FCSTD DOCUMENT  (FreeCAD 0.19R24276 (Git))
Label: Master_sketch_3_2
License: All rights reserved
LicenseURL: http://en.wikipedia.org/wiki/All_rights_reserved
objects: Sketcher::SketchObject×1, PartDesign::Body×1
note: 2 computed .brp shape members not serialized (recipe doc carries the construction recipe); baked Part::Feature solids carry a one-line shape summary decoded from their .brp

FEATURE [Sketcher::SketchObject] Sketch
  FullyConstrained = false
  MapMode = 5
  Support = -> [XY_Plane]
  sketch-geometry (199):
    g0: LineSegment StartX=-40 StartY=82 StartZ=0 EndX=40 EndY=82 EndZ=0
    g1: LineSegment StartX=40 StartY=82 StartZ=0 EndX=40 EndY=71 EndZ=0
    g2: LineSegment StartX=40 StartY=71 StartZ=0 EndX=-40 EndY=71 EndZ=0
    g3: LineSegment StartX=-40 StartY=71 StartZ=0 EndX=-40 EndY=82 EndZ=0
    g4: LineSegment StartX=-25 StartY=82 StartZ=0 EndX=-25 EndY=71 EndZ=0
    g5: LineSegment StartX=25 StartY=82 StartZ=0 EndX=25 EndY=71 EndZ=0
    g6: LineSegment StartX=-40 StartY=71 StartZ=0 EndX=-25 EndY=82 EndZ=0
    g7: LineSegment StartX=-40 StartY=82 StartZ=0 EndX=-25 EndY=71 EndZ=0
    g8: LineSegment StartX=25 StartY=71 StartZ=0 EndX=40 EndY=82 EndZ=0
    g9: LineSegment StartX=25 StartY=82 StartZ=0 EndX=40 EndY=71 EndZ=0
    g10: LineSegment StartX=-40 StartY=108 StartZ=0 EndX=40 EndY=108 EndZ=0
    g11: LineSegment StartX=40 StartY=108 StartZ=0 EndX=40 EndY=119 EndZ=0
    g12: LineSegment StartX=40 StartY=119 StartZ=0 EndX=-40 EndY=119 EndZ=0
    g13: LineSegment StartX=-40 StartY=119 StartZ=0 EndX=-40 EndY=108 EndZ=0
    g14: LineSegment StartX=-25 StartY=108 StartZ=0 EndX=-25 EndY=119 EndZ=0
    g15: LineSegment StartX=25 StartY=108 StartZ=0 EndX=25 EndY=119 EndZ=0
    g16: LineSegment StartX=-40 StartY=119 StartZ=0 EndX=-25 EndY=108 EndZ=0
    g17: LineSegment StartX=-40 StartY=108 StartZ=0 EndX=-25 EndY=119 EndZ=0
    g18: LineSegment StartX=25 StartY=119 StartZ=0 EndX=40 EndY=108 EndZ=0
    g19: LineSegment StartX=25 StartY=108 StartZ=0 EndX=40 EndY=119 EndZ=0
    g20: LineSegment StartX=-116.97 StartY=98 StartZ=0 EndX=25 EndY=98 EndZ=0
    g21: LineSegment StartX=25 StartY=98 StartZ=0 EndX=25 EndY=92 EndZ=0
    g22: LineSegment StartX=25 StartY=92 StartZ=0 EndX=-116.97 EndY=92 EndZ=0
    g23: LineSegment StartX=-116.97 StartY=92 StartZ=0 EndX=-116.97 EndY=98 EndZ=0
    g24: LineSegment StartX=-24 StartY=122 StartZ=0 EndX=-12.5 EndY=122 EndZ=0
    g25: LineSegment StartX=24 StartY=122 StartZ=0 EndX=24 EndY=70 EndZ=0
    g26: LineSegment StartX=24 StartY=70 StartZ=0 EndX=-24 EndY=70 EndZ=0
    g27: LineSegment StartX=12.5 StartY=122 StartZ=0 EndX=12.5 EndY=224.424 EndZ=0
    g28: LineSegment StartX=12.5 StartY=224.424 StartZ=0 EndX=-12.5 EndY=224.424 EndZ=0
    g29: LineSegment StartX=-12.5 StartY=224.424 StartZ=0 EndX=-12.5 EndY=122 EndZ=0
    g30: LineSegment StartX=61.35 StartY=170 StartZ=0 EndX=61.35 EndY=10 EndZ=0
    g31: LineSegment StartX=44.35 StartY=70 StartZ=0 EndX=44.35 EndY=102 EndZ=0
    g32: LineSegment StartX=26.35 StartY=70 StartZ=0 EndX=44.35 EndY=70 EndZ=0
    g33: LineSegment StartX=26.35 StartY=107 StartZ=0 EndX=44.35 EndY=107 EndZ=0
    g34: LineSegment StartX=44.35 StartY=102 StartZ=0 EndX=26.35 EndY=102 EndZ=0
    g35: LineSegment StartX=26.35 StartY=102 StartZ=0 EndX=26.35 EndY=107 EndZ=0
    g36: LineSegment StartX=44.35 StartY=107 StartZ=0 EndX=44.35 EndY=151 EndZ=0
    g37: LineSegment StartX=-115.97 StartY=100 StartZ=0 EndX=-99.97 EndY=100 EndZ=0
    g38: LineSegment StartX=-99.97 StartY=100 StartZ=0 EndX=-99.97 EndY=90 EndZ=0
    g39: LineSegment StartX=-99.97 StartY=90 StartZ=0 EndX=-115.97 EndY=90 EndZ=0
    g40: LineSegment StartX=-115.97 StartY=90 StartZ=0 EndX=-115.97 EndY=100 EndZ=0
    g41: LineSegment StartX=-110.97 StartY=90 StartZ=0 EndX=-104.97 EndY=90 EndZ=0
    g42: LineSegment StartX=-104.97 StartY=90 StartZ=0 EndX=-104.97 EndY=80 EndZ=0
    g43: LineSegment StartX=-104.97 StartY=80 StartZ=0 EndX=-110.97 EndY=80 EndZ=0
    g44: LineSegment StartX=-110.97 StartY=80 StartZ=0 EndX=-110.97 EndY=90 EndZ=0
    g45: LineSegment StartX=-123.97 StartY=80 StartZ=0 EndX=-91.97 EndY=80 EndZ=0
    g46: LineSegment StartX=-91.97 StartY=80 StartZ=0 EndX=-91.97 EndY=30 EndZ=0
    g47: LineSegment StartX=-91.97 StartY=30 StartZ=0 EndX=-123.97 EndY=30 EndZ=0
    g48: LineSegment StartX=-123.97 StartY=30 StartZ=0 EndX=-123.97 EndY=80 EndZ=0
    g49: LineSegment StartX=-40 StartY=239.89 StartZ=0 EndX=40 EndY=239.89 EndZ=0
    g50: LineSegment StartX=40 StartY=239.89 StartZ=0 EndX=40 EndY=228.89 EndZ=0
    g51: LineSegment StartX=-40 StartY=228.89 StartZ=0 EndX=-40 EndY=239.89 EndZ=0
    g52: LineSegment StartX=-25 StartY=239.89 StartZ=0 EndX=-25 EndY=228.89 EndZ=0
    g53: LineSegment StartX=25 StartY=239.89 StartZ=0 EndX=25 EndY=228.89 EndZ=0
    g54: LineSegment StartX=-40 StartY=228.89 StartZ=0 EndX=-25 EndY=239.89 EndZ=0
    g55: LineSegment StartX=-40 StartY=239.89 StartZ=0 EndX=-25 EndY=228.89 EndZ=0
    g56: LineSegment StartX=25 StartY=228.89 StartZ=0 EndX=40 EndY=239.89 EndZ=0
    g57: LineSegment StartX=25 StartY=239.89 StartZ=0 EndX=40 EndY=228.89 EndZ=0
    g58: LineSegment StartX=26.35 StartY=70 StartZ=0 EndX=26.35 EndY=10 EndZ=0
    g59: LineSegment StartX=26.35 StartY=10 StartZ=0 EndX=61.35 EndY=10 EndZ=0
    g60: LineSegment StartX=-26.35 StartY=70 StartZ=0 EndX=-61.35 EndY=70 EndZ=0
    g61: LineSegment StartX=-61.35 StartY=70 StartZ=0 EndX=-61.35 EndY=10 EndZ=0
    g62: LineSegment StartX=-61.35 StartY=10 StartZ=0 EndX=-26.35 EndY=10 EndZ=0
    g63: LineSegment StartX=-26.35 StartY=10 StartZ=0 EndX=-26.35 EndY=70 EndZ=0
    g64: LineSegment StartX=61.35 StartY=10 StartZ=0 EndX=-238.65 EndY=10 EndZ=0
    g65: LineSegment StartX=-238.65 StartY=10 StartZ=0 EndX=-238.65 EndY=0 EndZ=0
    g66: LineSegment StartX=-238.65 StartY=0 StartZ=0 EndX=61.35 EndY=0 EndZ=0
    g67: LineSegment StartX=61.35 StartY=0 StartZ=0 EndX=61.35 EndY=10 EndZ=0
    g68: LineSegment StartX=110 StartY=227.584 StartZ=0 EndX=190 EndY=227.584 EndZ=0
    g69: LineSegment StartX=190 StartY=227.584 StartZ=0 EndX=190 EndY=238.584 EndZ=0
    g70: LineSegment StartX=190 StartY=238.584 StartZ=0 EndX=110 EndY=238.584 EndZ=0
    g71: LineSegment StartX=110 StartY=238.584 StartZ=0 EndX=110 EndY=227.584 EndZ=0
    g72: LineSegment StartX=125 StartY=227.584 StartZ=0 EndX=125 EndY=238.584 EndZ=0
    g73: LineSegment StartX=175 StartY=227.584 StartZ=0 EndX=175 EndY=238.584 EndZ=0
    g74: LineSegment StartX=110 StartY=238.584 StartZ=0 EndX=125 EndY=227.584 EndZ=0
    g75: LineSegment StartX=110 StartY=227.584 StartZ=0 EndX=125 EndY=238.584 EndZ=0
    g76: LineSegment StartX=175 StartY=238.584 StartZ=0 EndX=190 EndY=227.584 EndZ=0
    g77: LineSegment StartX=175 StartY=227.584 StartZ=0 EndX=190 EndY=238.584 EndZ=0
    g78: LineSegment StartX=0 StartY=0 StartZ=0 EndX=0 EndY=224.424 EndZ=0
    g79: LineSegment StartX=150 StartY=253.536 StartZ=0 EndX=150 EndY=227.584 EndZ=0
    g80: LineSegment StartX=128.455 StartY=171.206 StartZ=0 EndX=171.545 EndY=171.206 EndZ=0
    g81: LineSegment StartX=171.545 StartY=253.536 StartZ=0 EndX=128.455 EndY=253.536 EndZ=0
    g82: LineSegment StartX=128.455 StartY=253.536 StartZ=0 EndX=128.455 EndY=171.206 EndZ=0
    g83: LineSegment StartX=-12.5 StartY=224.424 StartZ=0 EndX=204.13 EndY=224.424 EndZ=0
    g84: LineSegment StartX=204.13 StartY=224.424 StartZ=0 EndX=204.13 EndY=243.027 EndZ=0
    g85: LineSegment StartX=204.13 StartY=243.027 StartZ=0 EndX=-12.5 EndY=243.027 EndZ=0
    g86: LineSegment StartX=-12.5 StartY=243.027 StartZ=0 EndX=-12.5 EndY=224.424 EndZ=0
    g87: LineSegment StartX=171.545 StartY=253.536 StartZ=0 EndX=171.545 EndY=171.206 EndZ=0
    g88: LineSegment StartX=-190 StartY=228.217 StartZ=0 EndX=-110 EndY=228.217 EndZ=0
    g89: LineSegment StartX=-110 StartY=228.217 StartZ=0 EndX=-110 EndY=239.217 EndZ=0
    g90: LineSegment StartX=-110 StartY=239.217 StartZ=0 EndX=-190 EndY=239.217 EndZ=0
    g91: LineSegment StartX=-190 StartY=239.217 StartZ=0 EndX=-190 EndY=228.217 EndZ=0
    g92: LineSegment StartX=-175 StartY=228.217 StartZ=0 EndX=-175 EndY=239.217 EndZ=0
    g93: LineSegment StartX=-125 StartY=228.217 StartZ=0 EndX=-125 EndY=239.217 EndZ=0
    g94: LineSegment StartX=-190 StartY=239.217 StartZ=0 EndX=-175 EndY=228.217 EndZ=0
    g95: LineSegment StartX=-190 StartY=228.217 StartZ=0 EndX=-175 EndY=239.217 EndZ=0
    g96: LineSegment StartX=-125 StartY=239.217 StartZ=0 EndX=-110 EndY=228.217 EndZ=0
    g97: LineSegment StartX=-125 StartY=228.217 StartZ=0 EndX=-110 EndY=239.217 EndZ=0
    g98: LineSegment StartX=-194.17 StartY=244.672 StartZ=0 EndX=12.5 EndY=244.672 EndZ=0
    g99: LineSegment StartX=12.5 StartY=244.672 StartZ=0 EndX=12.5 EndY=223.501 EndZ=0
    g100: LineSegment StartX=12.5 StartY=223.501 StartZ=0 EndX=-194.17 EndY=223.501 EndZ=0
    g101: LineSegment StartX=-194.17 StartY=223.501 StartZ=0 EndX=-194.17 EndY=244.672 EndZ=0
    g102: LineSegment StartX=12.5 StartY=224.424 StartZ=0 EndX=-12.5 EndY=224.424 EndZ=0
    g103: LineSegment StartX=-12.5 StartY=224.424 StartZ=0 EndX=-12.5 EndY=249.397 EndZ=0
    g104: LineSegment StartX=-12.5 StartY=249.397 StartZ=0 EndX=12.5 EndY=249.397 EndZ=0
    g105: LineSegment StartX=12.5 StartY=249.397 StartZ=0 EndX=12.5 EndY=224.424 EndZ=0
    g106: LineSegment StartX=-168.275 StartY=254.074 StartZ=0 EndX=-131.725 EndY=254.074 EndZ=0
    g107: LineSegment StartX=-131.725 StartY=254.074 StartZ=0 EndX=-131.725 EndY=190.124 EndZ=0
    g108: LineSegment StartX=-131.725 StartY=190.124 StartZ=0 EndX=-168.275 EndY=190.124 EndZ=0
    g109: LineSegment StartX=-168.275 StartY=190.124 StartZ=0 EndX=-168.275 EndY=254.074 EndZ=0
    g110: LineSegment StartX=-150 StartY=228.217 StartZ=0 EndX=-150 EndY=254.074 EndZ=0
    g111: LineSegment StartX=40 StartY=228.89 StartZ=0 EndX=-40 EndY=228.89 EndZ=0
    g112: LineSegment StartX=-107.97 StartY=80 StartZ=0 EndX=-107.97 EndY=30 EndZ=0
    g113: LineSegment StartX=-107.97 StartY=80 StartZ=0 EndX=-107.97 EndY=90 EndZ=0
    g114: LineSegment StartX=-178 StartY=152 StartZ=0 EndX=-162 EndY=152 EndZ=0
    g115: LineSegment StartX=-162 StartY=152 StartZ=0 EndX=-162 EndY=142 EndZ=0
    g116: LineSegment StartX=-162 StartY=142 StartZ=0 EndX=-178 EndY=142 EndZ=0
    g117: LineSegment StartX=-178 StartY=142 StartZ=0 EndX=-178 EndY=152 EndZ=0
    g118: LineSegment StartX=-173 StartY=142 StartZ=0 EndX=-167 EndY=142 EndZ=0
    g119: LineSegment StartX=-167 StartY=142 StartZ=0 EndX=-167 EndY=132 EndZ=0
    g120: LineSegment StartX=-167 StartY=132 StartZ=0 EndX=-173 EndY=132 EndZ=0
    g121: LineSegment StartX=-173 StartY=132 StartZ=0 EndX=-173 EndY=142 EndZ=0
    g122: LineSegment StartX=-186 StartY=132 StartZ=0 EndX=-154 EndY=132 EndZ=0
    g123: LineSegment StartX=-154 StartY=132 StartZ=0 EndX=-154 EndY=82 EndZ=0
    g124: LineSegment StartX=-154 StartY=82 StartZ=0 EndX=-186 EndY=82 EndZ=0
    g125: LineSegment StartX=-186 StartY=82 StartZ=0 EndX=-186 EndY=132 EndZ=0
    g126: LineSegment StartX=-170 StartY=132 StartZ=0 EndX=-170 EndY=82 EndZ=0
    g127: LineSegment StartX=-170 StartY=111.828 StartZ=0 EndX=-170 EndY=142 EndZ=0
    g128: LineSegment StartX=-180 StartY=144 StartZ=0 EndX=-180 EndY=150 EndZ=0
    g129: LineSegment StartX=-24 StartY=70 StartZ=0 EndX=-24 EndY=122 EndZ=0
    g130: LineSegment StartX=-40 StartY=168 StartZ=0 EndX=40 EndY=168 EndZ=0
    g131: LineSegment StartX=40 StartY=168 StartZ=0 EndX=40 EndY=157 EndZ=0
    g132: LineSegment StartX=40 StartY=157 StartZ=0 EndX=-40 EndY=157 EndZ=0
    g133: LineSegment StartX=-40 StartY=157 StartZ=0 EndX=-40 EndY=168 EndZ=0
    g134: LineSegment StartX=-25 StartY=168 StartZ=0 EndX=-25 EndY=157 EndZ=0
    g135: LineSegment StartX=25 StartY=168 StartZ=0 EndX=25 EndY=157 EndZ=0
    g136: LineSegment StartX=-40 StartY=157 StartZ=0 EndX=-25 EndY=168 EndZ=0
    g137: LineSegment StartX=-40 StartY=168 StartZ=0 EndX=-25 EndY=157 EndZ=0
    g138: LineSegment StartX=25 StartY=157 StartZ=0 EndX=40 EndY=168 EndZ=0
    g139: LineSegment StartX=25 StartY=168 StartZ=0 EndX=40 EndY=157 EndZ=0
    g140: LineSegment StartX=44.35 StartY=151 StartZ=0 EndX=26.35 EndY=151 EndZ=0
    g141: LineSegment StartX=26.35 StartY=151 StartZ=0 EndX=26.35 EndY=156 EndZ=0
    g142: LineSegment StartX=26.35 StartY=156 StartZ=0 EndX=44.35 EndY=156 EndZ=0
    g143: LineSegment StartX=44.35 StartY=156 StartZ=0 EndX=44.35 EndY=170 EndZ=0
    g144: LineSegment StartX=44.35 StartY=170 StartZ=0 EndX=61.35 EndY=170 EndZ=0
    g145: LineSegment StartX=0 StartY=0 StartZ=0 EndX=7e-16 EndY=122 EndZ=0
    g146: LineSegment StartX=12.5 StartY=122 StartZ=0 EndX=24 EndY=122 EndZ=0
    g147: LineSegment StartX=20 StartY=168 StartZ=0 EndX=20 EndY=157 EndZ=0
    g148: LineSegment StartX=18.9042 StartY=140.952 StartZ=0 EndX=14.6064 EndY=140.952 EndZ=0
    g149: LineSegment StartX=14.6064 StartY=140.952 StartZ=0 EndX=14.6064 EndY=185.7 EndZ=0
    g150: LineSegment StartX=14.6064 StartY=185.7 StartZ=0 EndX=18.9042 EndY=185.7 EndZ=0
    g151: LineSegment StartX=18.9042 StartY=185.7 StartZ=0 EndX=18.9042 EndY=140.952 EndZ=0
    g152: LineSegment StartX=18.9042 StartY=140.952 StartZ=0 EndX=-22.7731 EndY=140.952 EndZ=0
    g153: LineSegment StartX=-22.7731 StartY=140.952 StartZ=0 EndX=-22.7731 EndY=185.7 EndZ=0
    g154: LineSegment StartX=-22.7731 StartY=185.7 StartZ=0 EndX=18.9042 EndY=185.7 EndZ=0
    g155: LineSegment StartX=18.9042 StartY=185.7 StartZ=0 EndX=18.9042 EndY=140.952 EndZ=0
    g156: LineSegment StartX=-180 StartY=150 StartZ=0 EndX=-18.2105 EndY=150 EndZ=0
    g157: LineSegment StartX=-18.2105 StartY=150 StartZ=0 EndX=-18.2105 EndY=144 EndZ=0
    g158: LineSegment StartX=-18.2105 StartY=144 StartZ=0 EndX=-180 EndY=144 EndZ=0
    g159: LineSegment StartX=-180 StartY=144 StartZ=0 EndX=-180 EndY=150 EndZ=0
    g160: LineSegment StartX=-30.1922 StartY=182.283 StartZ=0 EndX=177.476 EndY=182.283 EndZ=0
    g161: LineSegment StartX=177.476 StartY=182.283 StartZ=0 EndX=177.476 EndY=175.07 EndZ=0
    g162: LineSegment StartX=177.476 StartY=175.07 StartZ=0 EndX=-30.1922 EndY=175.07 EndZ=0
    g163: LineSegment StartX=-30.1922 StartY=175.07 StartZ=0 EndX=-30.1922 EndY=182.283 EndZ=0
    g164: LineSegment StartX=-172.187 StartY=204.388 StartZ=0 EndX=16.8782 EndY=204.388 EndZ=0
    g165: LineSegment StartX=16.8782 StartY=204.388 StartZ=0 EndX=16.8782 EndY=197.555 EndZ=0
    g166: LineSegment StartX=16.8782 StartY=197.555 StartZ=0 EndX=-172.187 EndY=197.555 EndZ=0
    g167: LineSegment StartX=-172.187 StartY=197.555 StartZ=0 EndX=-172.187 EndY=204.388 EndZ=0
    g168: LineSegment StartX=-266.032 StartY=240.888 StartZ=0 EndX=-250.032 EndY=240.888 EndZ=0
    g169: LineSegment StartX=-250.032 StartY=240.888 StartZ=0 EndX=-250.032 EndY=230.888 EndZ=0
    g170: LineSegment StartX=-250.032 StartY=230.888 StartZ=0 EndX=-266.032 EndY=230.888 EndZ=0
    g171: LineSegment StartX=-266.032 StartY=230.888 StartZ=0 EndX=-266.032 EndY=240.888 EndZ=0
    g172: LineSegment StartX=-261.032 StartY=230.888 StartZ=0 EndX=-255.032 EndY=230.888 EndZ=0
    g173: LineSegment StartX=-255.032 StartY=230.888 StartZ=0 EndX=-255.032 EndY=220.888 EndZ=0
    g174: LineSegment StartX=-255.032 StartY=220.888 StartZ=0 EndX=-261.032 EndY=220.888 EndZ=0
    g175: LineSegment StartX=-261.032 StartY=220.888 StartZ=0 EndX=-261.032 EndY=230.888 EndZ=0
    g176: LineSegment StartX=-274.032 StartY=220.888 StartZ=0 EndX=-242.032 EndY=220.888 EndZ=0
    g177: LineSegment StartX=-242.032 StartY=220.888 StartZ=0 EndX=-242.032 EndY=170.888 EndZ=0
    g178: LineSegment StartX=-242.032 StartY=170.888 StartZ=0 EndX=-274.032 EndY=170.888 EndZ=0
    g179: LineSegment StartX=-274.032 StartY=170.888 StartZ=0 EndX=-274.032 EndY=220.888 EndZ=0
    g180: LineSegment StartX=-258.032 StartY=220.888 StartZ=0 EndX=-258.032 EndY=170.888 EndZ=0
    g181: LineSegment StartX=-258.032 StartY=157.127 StartZ=0 EndX=-258.032 EndY=230.888 EndZ=0
    g182: LineSegment StartX=-268.032 StartY=232.888 StartZ=0 EndX=-268.032 EndY=238.888 EndZ=0
    g183: LineSegment StartX=-268.032 StartY=238.888 StartZ=0 EndX=-192.409 EndY=238.888 EndZ=0
    g184: LineSegment StartX=-268.032 StartY=232.888 StartZ=0 EndX=-192.409 EndY=232.888 EndZ=0
    g185: LineSegment StartX=-192.409 StartY=238.888 StartZ=0 EndX=-192.409 EndY=232.888 EndZ=0
    g186: LineSegment StartX=-3.12535 StartY=259.384 StartZ=0 EndX=3.12535 EndY=259.384 EndZ=0
    g187: LineSegment StartX=3.12535 StartY=259.384 StartZ=0 EndX=3.12535 EndY=248.133 EndZ=0
    g188: LineSegment StartX=3.12535 StartY=248.133 StartZ=0 EndX=-3.12535 EndY=248.133 EndZ=0
    g189: LineSegment StartX=-3.12535 StartY=248.133 StartZ=0 EndX=-3.12535 EndY=259.384 EndZ=0
    g190: LineSegment StartX=-153.066 StartY=190.124 StartZ=0 EndX=-145.852 EndY=190.124 EndZ=0
    g191: LineSegment StartX=-145.852 StartY=190.124 StartZ=0 EndX=-145.852 EndY=178.354 EndZ=0
    g192: LineSegment StartX=-145.852 StartY=178.354 StartZ=0 EndX=-153.066 EndY=178.354 EndZ=0
    g193: LineSegment StartX=-153.066 StartY=178.354 StartZ=0 EndX=-153.066 EndY=190.124 EndZ=0
    g194: LineSegment StartX=-149.269 StartY=175.697 StartZ=0 EndX=-123.29 EndY=164.988 EndZ=0
    g195: LineSegment StartX=-123.29 StartY=164.988 StartZ=0 EndX=-98.1269 EndY=176.245 EndZ=0
    g196: LineSegment StartX=-98.1269 StartY=176.245 StartZ=0 EndX=-76.1072 EndY=257.11 EndZ=0
    g197: LineSegment StartX=-76.1072 StartY=257.11 StartZ=0 EndX=-9.17807 EndY=272.887 EndZ=0
    g198: LineSegment StartX=-9.17807 StartY=272.887 StartZ=0 EndX=2.07637 EndY=264.856 EndZ=0
  constraints (521):
    c: Coincident(g0,g1)
    c: Coincident(g1,g2)
    c: Coincident(g2,g3)
    c: Coincident(g3,g0)
    c: Horizontal(g0)
    c: Horizontal(g2)
    c: Vertical(g1)
    c: Vertical(g3)
    c: PointOnObject(g4,g0)
    c: PointOnObject(g4,g2)
    c: Vertical(g4)
    c: PointOnObject(g5,g0)
    c: Vertical(g5)
    c: DistanceX(g2,g2) = 80
    c: DistanceX(g4,g5) = 50
    c: DistanceY(g3,g3) = 11
    c: Coincident(g6,g2)
    c: Coincident(g6,g4)
    c: Coincident(g7,g0)
    c: Coincident(g7,g4)
    c: Coincident(g8,g5)
    c: Coincident(g8,g0)
    c: Coincident(g9,g5)
    c: Coincident(g9,g1)
    c: DistanceX(g2,g4) = 15
    c: Coincident(g10,g11)
    c: Coincident(g11,g12)
    c: Coincident(g12,g13)
    c: Coincident(g13,g10)
    c: Horizontal(g10)
    c: Horizontal(g12)
    c: Vertical(g11)
    c: Vertical(g13)
    c: PointOnObject(g14,g10)
    c: PointOnObject(g14,g12)
    c: Vertical(g14)
    c: PointOnObject(g15,g10)
    c: Vertical(g15)
    c: Coincident(g16,g12)
    c: Coincident(g16,g14)
    c: Coincident(g17,g10)
    c: Coincident(g17,g14)
    c: Coincident(g18,g15)
    c: Coincident(g18,g10)
    c: Coincident(g19,g15)
    c: Coincident(g19,g11)
    c: Equal(g10,g2)
    c: Equal(g1,g11)
    c: Equal(g15,g11)
    c: Equal(g16,g7)
    c: Equal(g19,g8)
    c: Horizontal(g5,g1)
    c: Vertical(g4,g14)
    c: Coincident(g20,g21)
    c: Coincident(g21,g22)
    c: Coincident(g22,g23)
    c: Coincident(g23,g20)
    c: Horizontal(g20)
    c: Horizontal(g22)
    c: Vertical(g21)
    c: Vertical(g23)
    c: Coincident(g25,g26)
    c: Horizontal(g24)
    c: Horizontal(g26)
    c: Vertical(g25)
    c: DistanceX(g4,g26) = 1
    c: Coincident(g27,g28)
    c: Coincident(g28,g29)
    c: Horizontal(g28)
    c: Vertical(g27)
    c: Vertical(g29)
    c: DistanceX(g28,g27) = 25
    c: Vertical(g30)
    c: Vertical(g31)
    c: Horizontal(g32)
    c: Coincident(g34,g35)
    c: Coincident(g35,g33)
    c: Horizontal(g33)
    c: Horizontal(g34)
    c: Vertical(g35)
    c: Tangent(g31,g36)
    c: Vertical(g32,g34)
    c: Coincident(g32,g31)
    c: Coincident(g31,g34)
    c: Coincident(g33,g36)
    c: Coincident(g37,g38)
    c: Coincident(g38,g39)
    c: Coincident(g39,g40)
    c: Coincident(g40,g37)
    c: Horizontal(g37)
    c: Horizontal(g39)
    c: Vertical(g38)
    c: Vertical(g40)
    c: Coincident(g41,g42)
    c: Coincident(g42,g43)
    c: Coincident(g43,g44)
    c: Coincident(g44,g41)
    c: Horizontal(g41)
    c: Horizontal(g43)
    c: Vertical(g42)
    c: Vertical(g44)
    c: PointOnObject(g41,g39)
    c: Coincident(g45,g46)
    c: Coincident(g46,g47)
    c: Coincident(g47,g48)
    c: Coincident(g48,g45)
    c: Horizontal(g45)
    c: Horizontal(g47)
    c: Vertical(g46)
    c: Vertical(g48)
    c: Coincident(g111,g51)
    c: Coincident(g51,g49)
    c: Horizontal(g49)
    c: Vertical(g50)
    c: Vertical(g51)
    c: PointOnObject(g52,g49)
    c: Vertical(g52)
    c: PointOnObject(g53,g49)
    c: Vertical(g53)
    c: Coincident(g54,g111)
    c: Coincident(g54,g52)
    c: Coincident(g55,g49)
    c: Coincident(g55,g52)
    c: Coincident(g56,g53)
    c: Coincident(g57,g53)
    c: Coincident(g57,g50)
    c: Equal(g53,g50)
    c: Vertical(g111,g0)
    c: DistanceX(g5,g32) = 1.35
    c: DistanceX(g32,g32) = 18
    c: DistanceY(g31,g1) = 1
    c: DistanceY(g33,g10) = 1
    c: DistanceX(g25,g21) = 1
    c: DistanceX(g22,g39) = 1
    c: Coincident(g58,g59)
    c: Horizontal(g59)
    c: Vertical(g58)
    c: Coincident(g60,g61)
    c: Coincident(g61,g62)
    c: Coincident(g62,g63)
    c: Coincident(g63,g60)
    c: Horizontal(g60)
    c: Horizontal(g62)
    c: Vertical(g61)
    c: Vertical(g63)
    c: Horizontal(g62,g58)
    c: Equal(g62,g59)
    c: Coincident(g64,g65)
    c: Coincident(g65,g66)
    c: Coincident(g66,g67)
    c: Coincident(g67,g64)
    c: Horizontal(g64)
    c: Horizontal(g66)
    c: Vertical(g65)
    c: Vertical(g67)
    c: Coincident(g64,g59)
    c: Coincident(g68,g69)
    c: Coincident(g69,g70)
    c: Coincident(g70,g71)
    c: Coincident(g71,g68)
    c: Horizontal(g68)
    c: Vertical(g69)
    c: Vertical(g71)
    c: PointOnObject(g72,g68)
    c: PointOnObject(g72,g70)
    c: Vertical(g72)
    c: PointOnObject(g73,g68)
    c: Vertical(g73)
    c: Coincident(g74,g70)
    c: Coincident(g74,g72)
    c: Coincident(g75,g68)
    c: Coincident(g75,g72)
    c: Coincident(g76,g73)
    c: Coincident(g76,g68)
    c: Coincident(g77,g73)
    c: Coincident(g77,g69)
    c: Equal(g73,g69)
    c: Equal(g69,g50)
    c: Equal(g50,g71)
    c: Parallel(g77,g56)
    c: Parallel(g74,g55)
    c: Vertical(g78)
    c: Symmetric(g28,g27,g78)
    c: Vertical(g79)
    c: Symmetric(g68,g68,g79)
    c: DistanceX(g78,g79) = 150
    c: DistanceX(g60,g4) = 1.35
    c: Coincident(g81,g82)
    c: Coincident(g82,g80)
    c: Horizontal(g80)
    c: Horizontal(g81)
    c: Vertical(g82)
    c: Coincident(g83,g84)
    c: Coincident(g84,g85)
    c: Coincident(g85,g86)
    c: Coincident(g86,g83)
    c: Horizontal(g83)
    c: Horizontal(g85)
    c: Vertical(g84)
    c: Vertical(g86)
    c: Coincident(g83,g28)
    c: Vertical(g87)
    c: Coincident(g87,g80)
    c: Coincident(g81,g87)
    c: Horizontal(g60,g32)
    c: Coincident(g88,g89)
    c: Coincident(g89,g90)
    c: Coincident(g90,g91)
    c: Coincident(g91,g88)
    c: Horizontal(g88)
    c: Horizontal(g90)
    c: Vertical(g89)
    c: Vertical(g91)
    c: PointOnObject(g92,g88)
    c: PointOnObject(g92,g90)
    c: Vertical(g92)
    c: PointOnObject(g93,g88)
    c: Vertical(g93)
    c: Coincident(g94,g90)
    c: Coincident(g94,g92)
    c: Coincident(g95,g88)
    c: Coincident(g95,g92)
    c: Coincident(g96,g93)
    c: Coincident(g96,g88)
    c: Coincident(g97,g93)
    c: Coincident(g97,g89)
    c: Equal(g93,g89)
    c: Equal(g89,g50)
    c: Parallel(g97,g56)
    c: Parallel(g95,g54)
    c: Coincident(g98,g99)
    c: Coincident(g99,g100)
    c: Coincident(g100,g101)
    c: Coincident(g101,g98)
    c: Horizontal(g98)
    c: Horizontal(g100)
    c: Vertical(g99)
    c: Vertical(g101)
    c: Coincident(g102,g103)
    c: Coincident(g103,g104)
    c: Coincident(g104,g105)
    c: Coincident(g105,g102)
    c: Horizontal(g102)
    c: Horizontal(g104)
    c: Vertical(g103)
    c: Vertical(g105)
    c: Coincident(g102,g27)
    c: Vertical(g98,g104)
    c: Vertical(g102,g28)
    c: Coincident(g106,g107)
    c: Coincident(g107,g108)
    c: Coincident(g108,g109)
    c: Coincident(g109,g106)
    c: Horizontal(g106)
    c: Horizontal(g108)
    c: Vertical(g107)
    c: Vertical(g109)
    c: Vertical(g110)
    c: Symmetric(g88,g88,g110)
    c: Symmetric(g106,g106,g110)
    c: DistanceX(g110,g78) = 150
    c: Symmetric(g81,g81,g79)
    c: Vertical(g112)
    c: Symmetric(g47,g46,g112)
    c: Symmetric(g43,g42,g112)
    c: DistanceX(g47,g47) = 32
    c: Coincident(g113,g112)
    c: Vertical(g113)
    c: Symmetric(g39,g38,g113)
    c: DistanceX(g112,g78) = 107.97
    c: DistanceX(g66,g66) = 300
    c: DistanceX(g80,g80) = 43.09
    c: DistanceX(g108,g108) = 36.55
    c: DistanceX(g69,g84) = 14.13
    c: DistanceX(g100,g88) = 4.17
    c: Coincident(g78,g-1)
    c: DistanceX(g70,g70) = 80
    c: Horizontal(g66,g-1)
    c: DistanceY(g67,g67) = 10
    c: DistanceY(g61,g61) = 60
    c: Coincident(g58,g32)
    c: DistanceX(g61,g62) = 35
    c: DistanceY(g48,g48) = 50
    c: DistanceY(g-1,g112) = 30
    c: Horizontal(g43,g45)
    c: DistanceX(g43,g42) = 6
    c: DistanceX(g39,g39) = 16
    c: DistanceY(g45,g39) = 10
    c: DistanceY(g40,g40) = 10
    c: DistanceY(g23,g23) = 6
    c: Coincident(g114,g115)
    c: Coincident(g115,g116)
    c: Coincident(g116,g117)
    c: Coincident(g117,g114)
    c: Horizontal(g114)
    c: Horizontal(g116)
    c: Vertical(g115)
    c: Vertical(g117)
    c: Coincident(g118,g119)
    c: Coincident(g119,g120)
    c: Coincident(g120,g121)
    c: Coincident(g121,g118)
    c: Horizontal(g118)
    c: Horizontal(g120)
    c: Vertical(g119)
    c: Vertical(g121)
    c: PointOnObject(g118,g116)
    c: Coincident(g122,g123)
    c: Coincident(g123,g124)
    c: Coincident(g124,g125)
    c: Coincident(g125,g122)
    c: Horizontal(g122)
    c: Horizontal(g124)
    c: Vertical(g123)
    c: Vertical(g125)
    c: Vertical(g126)
    c: Symmetric(g124,g123,g126)
    c: Symmetric(g120,g119,g126)
    c: Equal(g47,g124) = 32
    c: Vertical(g127)
    c: Symmetric(g116,g115,g127)
    c: Equal(g48,g125) = 50
    c: Horizontal(g120,g122)
    c: DistanceX(g120,g119) = 6
    c: Equal(g39,g116) = 16
    c: DistanceY(g122,g116) = 10
    c: Equal(g40,g117) = 10
    c: Vertical(g127,g126)
    c: Vertical(g128)
    c: DistanceY(g128,g128) = 6
    c: DistanceY(g116,g128) = 2
    c: DistanceX(g126,g-1) = 170
    c: DistanceX(g128,g114) = 2
    c: DistanceY(g-1,g126) = 82
    c: Coincident(g59,g30)
    c: DistanceY(g30,g30) = 160
    c: DistanceY(g31,g31) = 32
    c: DistanceY(g36,g36) = 44
    c: DistanceY(g35,g35) = 5
    c: DistanceX(g26,g26) = 48
    c: DistanceY(g25,g25) = 52
    c: Horizontal(g25,g32)
    c: Coincident(g129,g26)
    c: Coincident(g129,g24)
    c: Vertical(g129)
    c: DistanceY(g39,g22) = 2
    c: Coincident(g24,g29)
    c: Coincident(g130,g131)
    c: Coincident(g131,g132)
    c: Coincident(g132,g133)
    c: Coincident(g133,g130)
    c: Horizontal(g130)
    c: Horizontal(g132)
    c: Vertical(g131)
    c: Vertical(g133)
    c: PointOnObject(g134,g130)
    c: PointOnObject(g134,g132)
    c: Vertical(g134)
    c: PointOnObject(g135,g130)
    c: Vertical(g135)
    c: Coincident(g136,g132)
    c: Coincident(g136,g134)
    c: Coincident(g137,g130)
    c: Coincident(g137,g134)
    c: Coincident(g138,g135)
    c: Coincident(g138,g130)
    c: Coincident(g139,g135)
    c: Coincident(g139,g131)
    c: Equal(g135,g131)
    c: Equal(g133,g13)
    c: Equal(g132,g10)
    c: Vertical(g132,g12)
    c: Equal(g136,g17)
    c: Equal(g138,g19)
    c: Coincident(g111,g50)
    c: Coincident(g49,g50)
    c: Coincident(g56,g49)
    c: Equal(g56,g138)
    c: Equal(g54,g136)
    c: Equal(g131,g50)
    c: Equal(g111,g132)
    c: Horizontal(g111)
    c: Coincident(g140,g141)
    c: Coincident(g141,g142)
    c: Horizontal(g140)
    c: Horizontal(g142)
    c: Vertical(g141)
    c: Coincident(g140,g36)
    c: Vertical(g140,g33)
    c: Equal(g35,g141)
    c: Coincident(g143,g142)
    c: Vertical(g143)
    c: Coincident(g144,g143)
    c: Coincident(g144,g30)
    c: Horizontal(g144)
    c: Vertical(g142,g36)
    c: DistanceY(g141,g131) = 1
    c: Coincident(g145,g-1)
    c: Symmetric(g24,g25,g145)
    c: Symmetric(g24,g27,g145)
    c: Coincident(g146,g27)
    c: Coincident(g146,g25)
    c: Horizontal(g24,g27)
    c: Vertical(g147)
    c: PointOnObject(g147,g130)
    c: PointOnObject(g147,g132)
    c: DistanceX(g147,g135) = 5
    c: Coincident(g148,g149)
    c: Coincident(g149,g150)
    c: Coincident(g150,g151)
    c: Coincident(g151,g148)
    c: Horizontal(g148)
    c: Horizontal(g150)
    c: Vertical(g149)
    c: Vertical(g151)
    c: Coincident(g152,g153)
    c: Coincident(g153,g154)
    c: Coincident(g154,g155)
    c: Coincident(g155,g152)
    c: Horizontal(g152)
    c: Horizontal(g154)
    c: Vertical(g153)
    c: Coincident(g152,g148)
    c: Coincident(g156,g157)
    c: Coincident(g157,g158)
    c: Coincident(g158,g159)
    c: Coincident(g159,g156)
    c: Horizontal(g156)
    c: Horizontal(g158)
    c: Vertical(g157)
    c: Coincident(g156,g128)
    c: Coincident(g158,g128)
    c: Coincident(g150,g154)
    c: Horizontal(g51,g52)
    c: Coincident(g160,g161)
    c: Coincident(g161,g162)
    c: Coincident(g162,g163)
    c: Coincident(g163,g160)
    c: Horizontal(g160)
    c: Horizontal(g162)
    c: Vertical(g161)
    c: Vertical(g163)
    c: Coincident(g164,g165)
    c: Coincident(g165,g166)
    c: Coincident(g166,g167)
    c: Coincident(g167,g164)
    c: Horizontal(g164)
    c: Horizontal(g166)
    c: Vertical(g165)
    c: Vertical(g167)
    c: Coincident(g168,g169)
    c: Coincident(g169,g170)
    c: Coincident(g170,g171)
    c: Coincident(g171,g168)
    c: Horizontal(g168)
    c: Horizontal(g170)
    c: Vertical(g169)
    c: Vertical(g171)
    c: Coincident(g172,g173)
    c: Coincident(g173,g174)
    c: Coincident(g174,g175)
    c: Coincident(g175,g172)
    c: Horizontal(g172)
    c: Horizontal(g174)
    c: Vertical(g173)
    c: Vertical(g175)
    c: PointOnObject(g172,g170)
    c: Coincident(g176,g177)
    c: Coincident(g177,g178)
    c: Coincident(g178,g179)
    c: Coincident(g179,g176)
    c: Horizontal(g176)
    c: Horizontal(g178)
    c: Vertical(g177)
    c: Vertical(g179)
    c: Vertical(g180)
    c: Symmetric(g178,g177,g180)
    c: Symmetric(g174,g173,g180)
    c: Vertical(g181)
    c: Symmetric(g170,g169,g181)
    c: Horizontal(g174,g176)
    c: DistanceX(g174,g173) = 6
    c: DistanceY(g176,g170) = 10
    c: Vertical(g181,g180)
    c: Vertical(g182)
    c: Equal(g128,g182) = 6
    c: DistanceY(g170,g182) = 2
    c: DistanceX(g182,g168) = 2
    c: Equal(g177,g125)
    c: Equal(g169,g115)
    c: Equal(g168,g114)
    c: Equal(g178,g122)
    c: Equal(g10,g88)
    c: Coincident(g183,g182)
    c: Horizontal(g183)
    c: Coincident(g184,g182)
    c: Horizontal(g184)
    c: Coincident(g185,g183)
    c: Coincident(g185,g184)
    c: Vertical(g185)
    c: Coincident(g186,g187)
    c: Coincident(g187,g188)
    c: Coincident(g188,g189)
    c: Coincident(g189,g186)
    c: Horizontal(g186)
    c: Horizontal(g188)
    c: Vertical(g187)
    c: Vertical(g189)
    c: Coincident(g190,g191)
    c: Coincident(g191,g192)
    c: Coincident(g192,g193)
    c: Coincident(g193,g190)
    c: Horizontal(g190)
    c: Horizontal(g192)
    c: Vertical(g191)
    c: Vertical(g193)
    c: PointOnObject(g190,g108)
    c: Coincident(g195,g194)
    c: Coincident(g196,g195)
    c: Coincident(g197,g196)
    c: Coincident(g198,g197)
FEATURE [PartDesign::Body] Body
  Group = -> [Sketch]
  Origin = -> Origin
